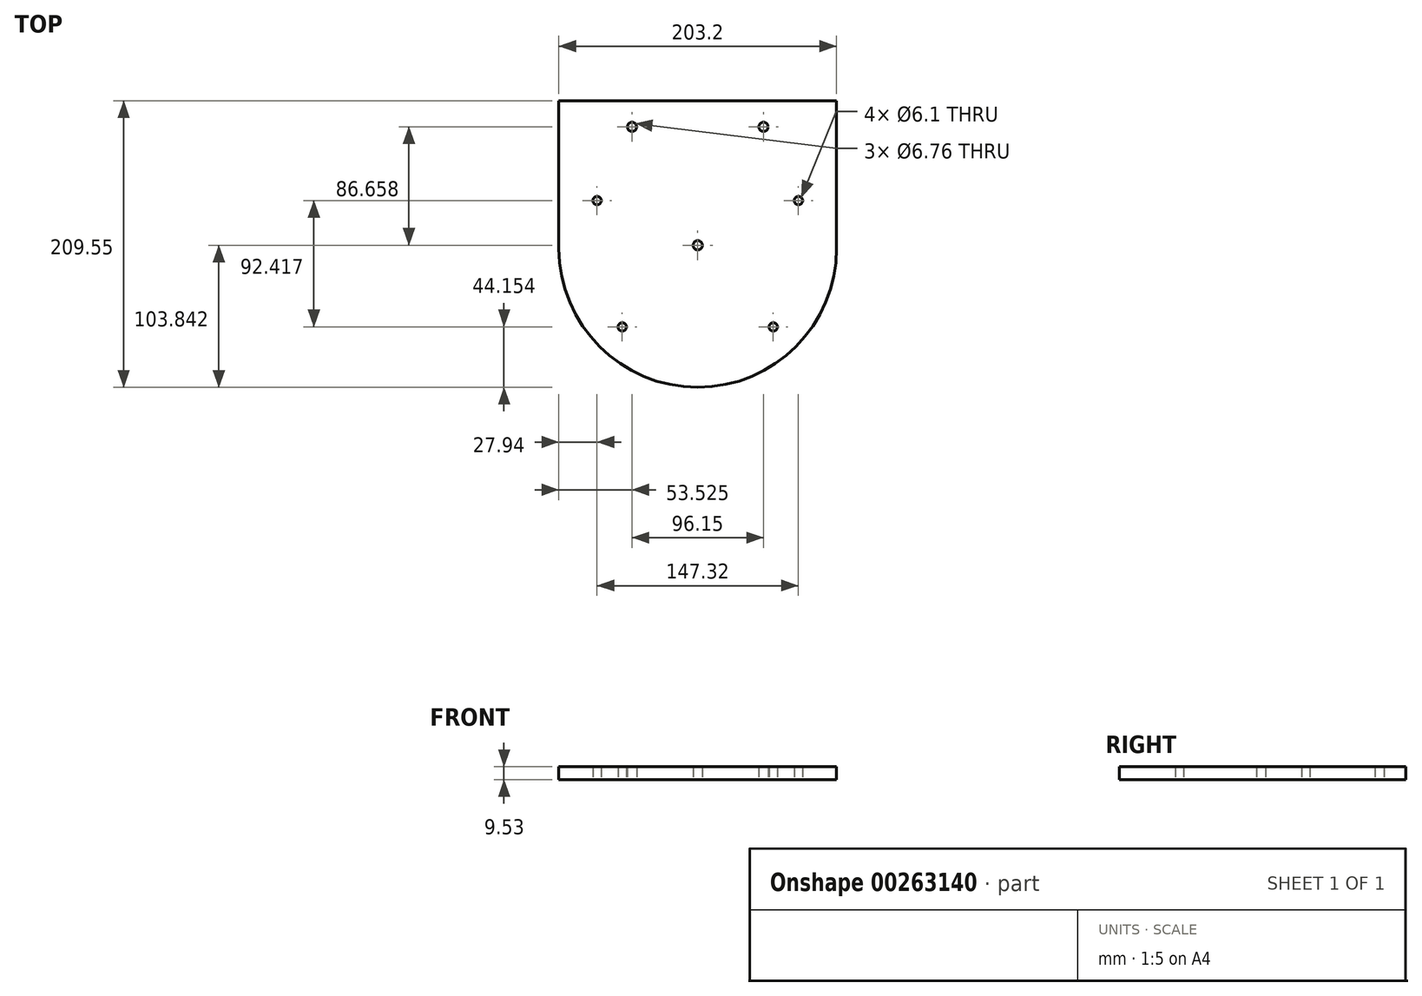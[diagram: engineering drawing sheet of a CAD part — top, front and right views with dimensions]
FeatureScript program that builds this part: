
annotation { "Feature Type Name" : "Feature", "Feature Type Description" : "" }
export const myFeature = defineFeature(function(context is Context, id is Id, definition is map)
    precondition{}
    {
        {
            var Q0;
            Q0=qCreatedBy(makeId("Top.planeOp"),FACE);
            var sketch = newSketch(context, id + "F0", { "sketchPlane" : qUnion([Q0])});
            skLineSegment(sketch, "E0", {"start": v(0, 107.95) * mm, "end": v(0, -101.6) * mm, "construction": true});
            skLineSegment(sketch, "E1.0", {"start": v(0, 2.24) * mm, "end": v(-48.08, 88.9) * mm, "construction": true});
            skLineSegment(sketch, "E1.1", {"start": v(-48.08, 88.9) * mm, "end": v(48.07, 88.9) * mm, "construction": true});
            skLineSegment(sketch, "E1.2", {"start": v(48.08, 88.9) * mm, "end": v(0, 2.24) * mm, "construction": true});
            skLineSegment(sketch, "E2", {"start": v(0, -57.45) * mm, "end": v(-55.24, -57.45) * mm, "construction": true});
            skLineSegment(sketch, "E3", {"start": v(-55.24, -57.45) * mm, "end": v(-73.66, 34.97) * mm, "construction": true});
            skArc(sketch, "E4", {"start": v(-101.6, 0) * mm, "mid": v(0, -101.6) * mm, "end": v(101.6, 0) * mm});
            skLineSegment(sketch, "E5", {"start": v(-101.6, 107.95) * mm, "end": v(-101.6, 0) * mm});
            skLineSegment(sketch, "E6", {"start": v(101.6, 107.95) * mm, "end": v(101.6, 0) * mm});
            skLineSegment(sketch, "E7", {"start": v(-101.6, 107.95) * mm, "end": v(101.6, 107.95) * mm});
            skLineSegment(sketch, "E8", {"start": v(0, 124.57) * mm, "end": v(101.6, 124.57) * mm, "construction": true});
            skLineSegment(sketch, "E9", {"start": v(0, 124.57) * mm, "end": v(-101.6, 124.57) * mm, "construction": true});
            skLineSegment(sketch, "E10", {"start": v(-73.66, 34.97) * mm, "end": v(0, 34.97) * mm, "construction": true});
            skLineSegment(sketch, "E11.MirrorCS", {"start": v(0, -57.45) * mm, "end": v(55.25, -57.45) * mm, "construction": true});
            skLineSegment(sketch, "E12.MirrorCS", {"start": v(55.25, -57.45) * mm, "end": v(73.66, 34.97) * mm, "construction": true});
            skLineSegment(sketch, "E13.MirrorCS", {"start": v(73.66, 34.97) * mm, "end": v(0, 34.97) * mm, "construction": true});
            skSolve(sketch);
        }
        {
            var Q0;
            Q0=makeQuery(id+"F0.imprint","IMPRINT",FACE,{"disambiguationData":[TD([[makeQuery(id+"F0.imprint","IMPRINT",EDGE,{"derivedFrom":sQuery(id+"F0.wireOp",EDGE,"E4")}),1.0]])]});
            extrude(context, id + "F1", {"entities" : qUnion([Q0]), "depth" : 9.52 * mm, "offsetDistance" : 25.4 * mm});
        }
        {
            var Q0;
            Q0=sQuery(id+"F0.wireOp",VERTEX,"E3.end");
            var Q1;
            Q1=sQuery(id+"F0.wireOp",VERTEX,"E12.MirrorCS.end");
            var Q2;
            Q2=sQuery(id+"F0.wireOp",VERTEX,"E3.start");
            var Q3;
            Q3=sQuery(id+"F0.wireOp",VERTEX,"E11.MirrorCS.end");
            var Q4;
            Q4=makeQuery(id+"F1.opExtrude","SWEPT_BODY",BODY,{"disambiguationData":[OSD([sQuery(id+"F0.wireOp",EDGE,"E4"),sQuery(id+"F0.wireOp",EDGE,"E5"),sQuery(id+"F0.wireOp",EDGE,"E6"),sQuery(id+"F0.wireOp",EDGE,"E7")])]});
            hole(context, id + "F2", {"style" : HoleStyle.SIMPLE, "endStyle" : HoleEndStyle.THROUGH, "oppositeDirection" : true, "holeDiameter" : 6.1 * mm, "majorDiameter" : 6.35 * mm, "isTappedThrough" : true, "tappedDepth" : 12.7 * mm, "tapClearance" : 3, "locations" : qUnion([Q0, Q1, Q2, Q3]), "scope" : qUnion([Q4])});
        }
        {
            var Q0;
            Q0=sQuery(id+"F0.wireOp",VERTEX,"E1.1.start");
            var Q1;
            Q1=sQuery(id+"F0.wireOp",VERTEX,"E1.2.end");
            var Q2;
            Q2=sQuery(id+"F0.wireOp",VERTEX,"E1.2.start");
            var Q3;
            Q3=makeQuery(id+"F1.opExtrude","SWEPT_BODY",BODY,{"disambiguationData":[OSD([sQuery(id+"F0.wireOp",EDGE,"E4"),sQuery(id+"F0.wireOp",EDGE,"E5"),sQuery(id+"F0.wireOp",EDGE,"E6"),sQuery(id+"F0.wireOp",EDGE,"E7")])]});
            hole(context, id + "F3", {"style" : HoleStyle.SIMPLE, "endStyle" : HoleEndStyle.THROUGH, "oppositeDirection" : true, "standardTappedOrClearance" : lookupTablePath({ "standard" : "ANSI", "fit" : "Normal (ASME)", "size" : "1/4", "type" : "Clearance" }), "standardBlindInLast" : lookupTablePath({ "fit" : "Free", "standard" : "ANSI", "size" : "1/4", "type" : "Clearance" }), "holeDiameter" : 6.76 * mm, "majorDiameter" : 6.35 * mm, "isTappedThrough" : true, "tappedDepth" : 12.7 * mm, "tapClearance" : 3, "locations" : qUnion([Q0, Q1, Q2]), "scope" : qUnion([Q3])});
        }
    });
